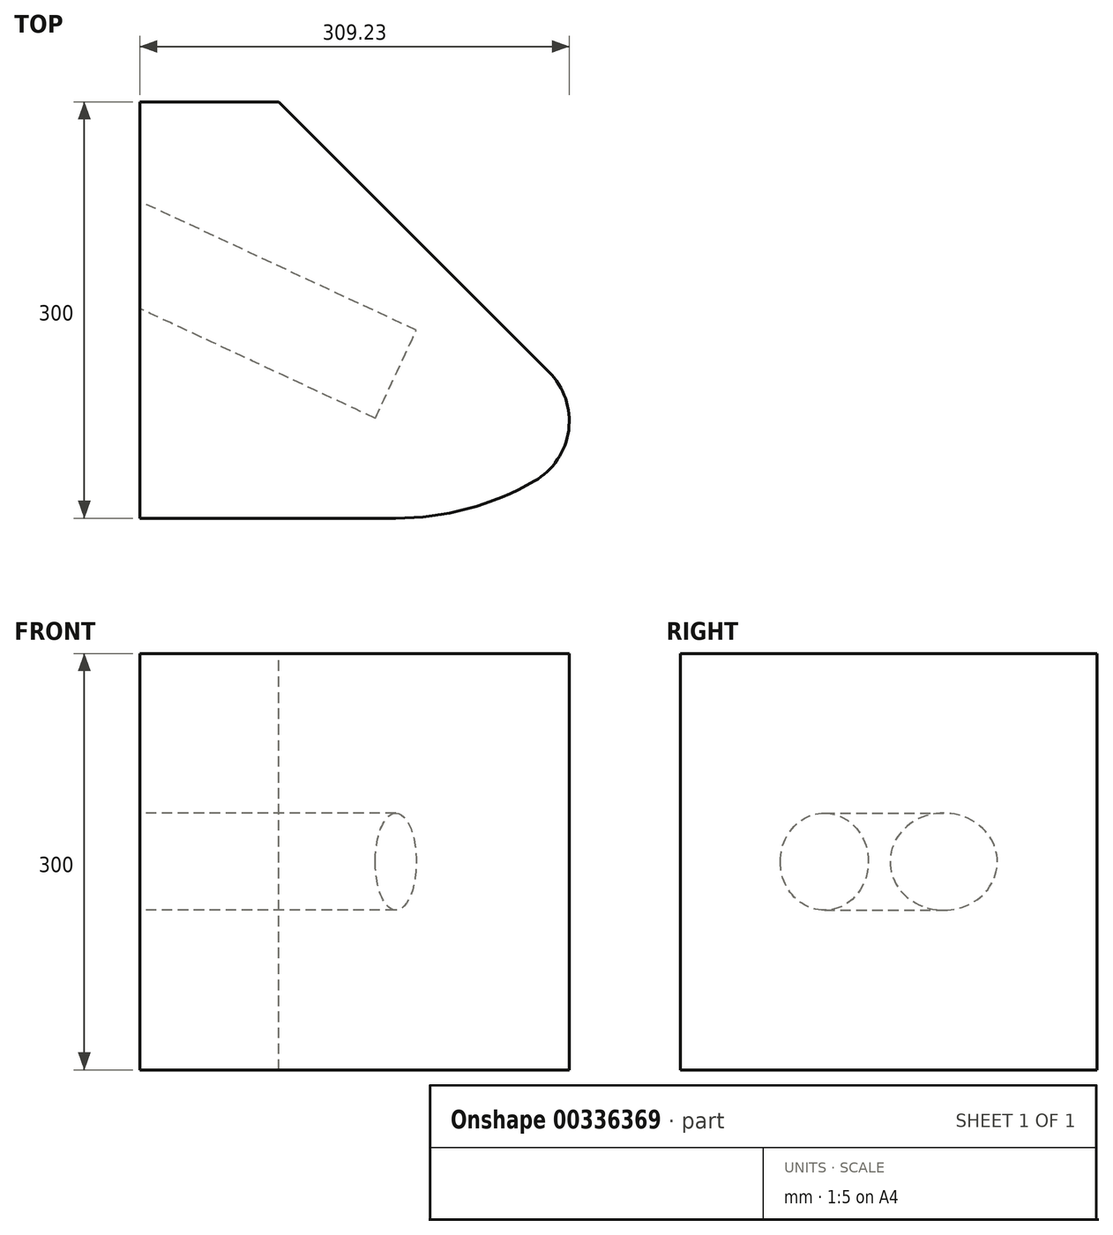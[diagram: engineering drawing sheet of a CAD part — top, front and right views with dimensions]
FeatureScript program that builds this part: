
annotation { "Feature Type Name" : "Feature", "Feature Type Description" : "" }
export const myFeature = defineFeature(function(context is Context, id is Id, definition is map)
    precondition{}
    {
        {
            var Q0;
            Q0=qCreatedBy(makeId("Top.planeOp"),FACE);
            var sketch = newSketch(context, id + "F0", { "sketchPlane" : qUnion([Q0])});
            skLineSegment(sketch, "E0", {"start": v(0, 0) * mm, "end": v(280, 0) * mm});
            skLineSegment(sketch, "E1", {"start": v(0, 0) * mm, "end": v(0, 300) * mm});
            skLineSegment(sketch, "E2", {"start": v(0, 300) * mm, "end": v(100, 300) * mm});
            skLineSegment(sketch, "E3", {"start": v(100, 300) * mm, "end": v(333.35, 66.65) * mm});
            skLineSegment(sketch, "E4", {"start": v(333.35, 66.65) * mm, "end": v(280, 0) * mm});
            skSolve(sketch);
        }
        {
            var Q0;
            Q0=makeQuery(id+"F0.imprint","IMPRINT",FACE,{"disambiguationData":[TD([[makeQuery(id+"F0.imprint","IMPRINT",EDGE,{"derivedFrom":sQuery(id+"F0.wireOp",EDGE,"E0")}),1.0]])]});
            extrude(context, id + "F1", {"entities" : qUnion([Q0]), "oppositeDirection" : true, "depth" : 300 * mm});
        }
        {
            var Q0;
            Q0=makeQuery(id+"F1.opExtrude","SWEPT_EDGE",EDGE,{"disambiguationData":[OSD([sQuery(id+"F0.wireOp",EDGE,"E0"),sQuery(id+"F0.wireOp",EDGE,"E4")])]});
            fillet(context, id + "F2", {"entities" : qUnion([Q0]), "radius" : 200 * mm, "tangentPropagation" : true, "allowEdgeOverflow" : false});
        }
        {
            var Q0;
            Q0=makeQuery(id+"F2.opFillet","BLEND_EDGE",EDGE,{"blendedFrom":[makeQuery(id+"F1.opExtrude","SWEPT_EDGE",EDGE,{"disambiguationData":[OSD([sQuery(id+"F0.wireOp",EDGE,"E0"),sQuery(id+"F0.wireOp",EDGE,"E4")])]}),makeQuery(id+"F1.opExtrude","SWEPT_FACE",FACE,{"disambiguationData":[OSD([sQuery(id+"F0.wireOp",EDGE,"E3")])]})],"blendedInto":[makeQuery(id+"F1.opExtrude","SWEPT_FACE",FACE,{"disambiguationData":[OSD([sQuery(id+"F0.wireOp",EDGE,"E3")])]})]});
            fillet(context, id + "F3", {"entities" : qUnion([Q0]), "radius" : 50 * mm, "tangentPropagation" : true, "allowEdgeOverflow" : false});
        }
        {
            var Q0;
            Q0=makeQuery(id+"F1.opExtrude","SWEPT_EDGE",EDGE,{"disambiguationData":[OSD([sQuery(id+"F0.wireOp",EDGE,"E1"),sQuery(id+"F0.wireOp",EDGE,"E2")])]});
            cPlane(context, id + "F4", {"entities" : qUnion([Q0]), "cplaneType" : CPlaneType.LINE_ANGLE, "offset" : 25 * mm, "angle" : 155 * degree, "width" : 150 * mm, "height" : 150 * mm});
        }
        {
            var Q0;
            Q0=qCreatedBy(id+"F4.planeOp",FACE);
            var sketch = newSketch(context, id + "F5", { "sketchPlane" : qUnion([Q0])});
            skCircle(sketch, "E5", {"center": v(-171.9, -150) * mm, "radius": 35 * mm});
            skSolve(sketch);
        }
        {
            var Q0;
            Q0=qSketchRegion(id+"F5",true);
            extrude(context, id + "F6", {"entities" : qUnion([Q0]), "operationType" : NewBodyOperationType.REMOVE, "oppositeDirection" : true, "depth" : 250 * mm});
        }
    });
